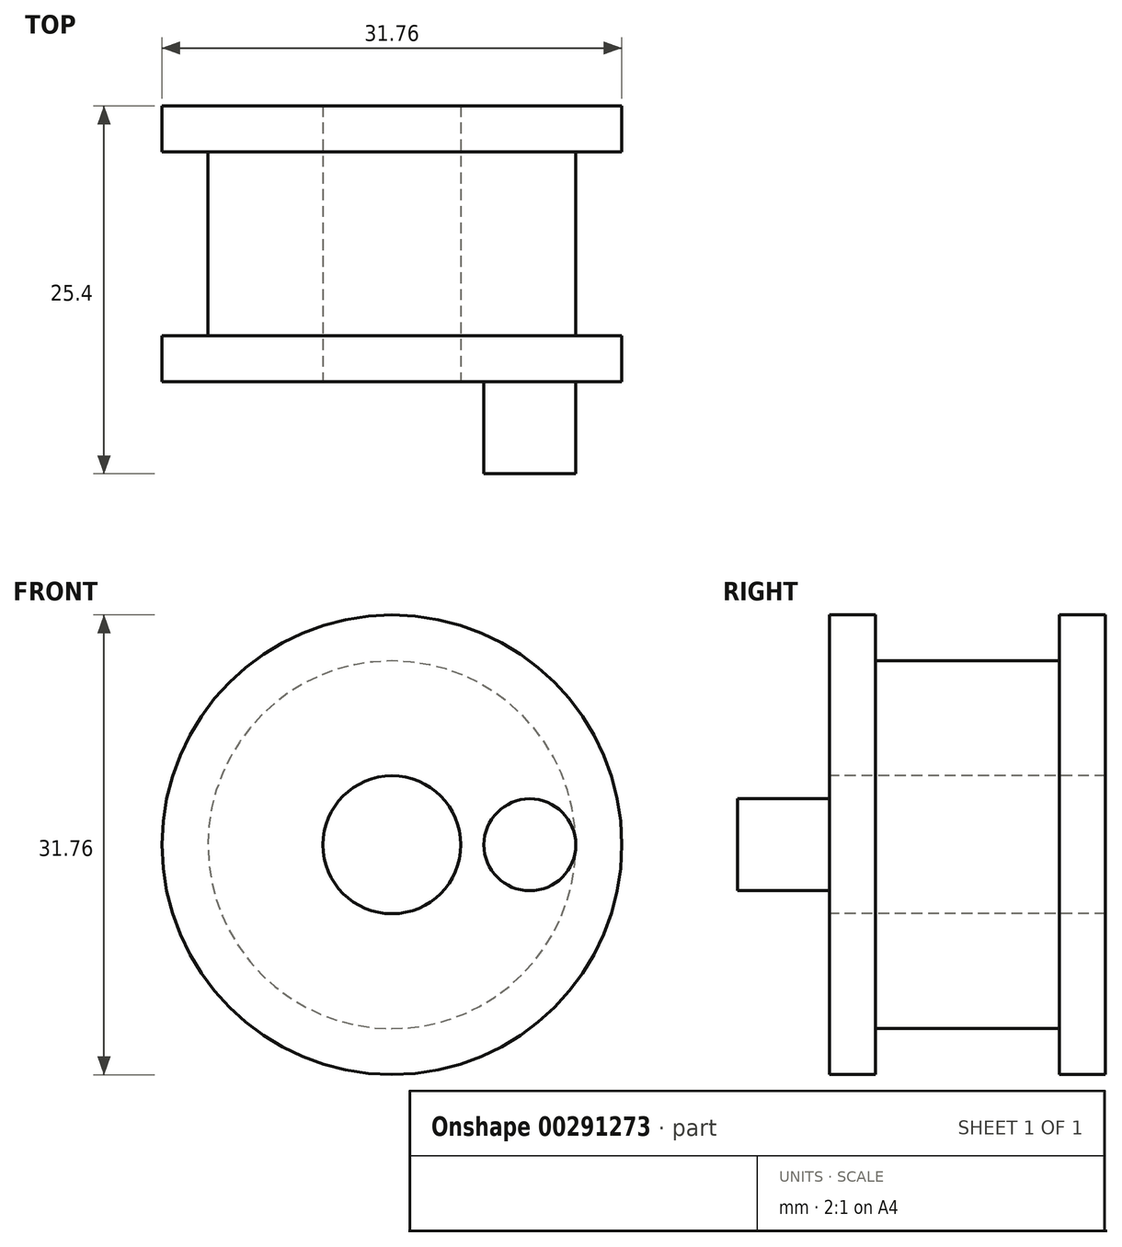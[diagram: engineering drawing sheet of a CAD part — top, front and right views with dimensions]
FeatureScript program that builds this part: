
annotation { "Feature Type Name" : "Feature", "Feature Type Description" : "" }
export const myFeature = defineFeature(function(context is Context, id is Id, definition is map)
    precondition{}
    {
        {
            var Q0;
            Q0=qCreatedBy(makeId("Right.planeOp"),FACE);
            var sketch = newSketch(context, id + "F0", { "sketchPlane" : qUnion([Q0])});
            skLineSegment(sketch, "E0", {"start": v(0, 0) * mm, "end": v(0, 4.76) * mm});
            skLineSegment(sketch, "E1", {"start": v(0, 4.76) * mm, "end": v(19.05, 4.76) * mm});
            skLineSegment(sketch, "E2", {"start": v(19.05, 4.76) * mm, "end": v(19.05, 15.88) * mm});
            skLineSegment(sketch, "E3", {"start": v(19.05, 15.88) * mm, "end": v(15.88, 15.88) * mm});
            skLineSegment(sketch, "E4", {"start": v(15.88, 15.88) * mm, "end": v(15.88, 12.7) * mm});
            skLineSegment(sketch, "E5", {"start": v(15.88, 12.7) * mm, "end": v(3.17, 12.7) * mm});
            skLineSegment(sketch, "E6", {"start": v(3.17, 12.7) * mm, "end": v(3.17, 15.88) * mm});
            skLineSegment(sketch, "E7", {"start": v(3.17, 15.88) * mm, "end": v(0, 15.88) * mm});
            skLineSegment(sketch, "E8", {"start": v(0, 15.88) * mm, "end": v(0, 4.76) * mm});
            skLineSegment(sketch, "E9", {"start": v(0, 0) * mm, "end": v(30.3, 0) * mm});
            skSolve(sketch);
        }
        {
            var Q0;
            Q0 = qSketchRegion(id + "F0", true);
            var Q1;
            Q1=sQuery(id+"F0.wireOp",EDGE,"E9");
            revolve(context, id + "F1", {"entities" : qUnion([Q0]), "axis" : qUnion([Q1]), "revolveType" : RevolveType.FULL});
        }
        {
            var Q0;
            Q0=qCreatedBy(makeId("Front.planeOp"),FACE);
            var sketch = newSketch(context, id + "F2", { "sketchPlane" : qUnion([Q0])});
            skCircle(sketch, "E10", {"center": v(9.53, 0) * mm, "radius": 3.18 * mm});
            skSolve(sketch);
        }
        {
            var Q0;
            Q0 = qSketchRegion(id + "F2", true);
            extrude(context, id + "F3", {"entities" : qUnion([Q0]), "operationType" : NewBodyOperationType.ADD, "depth" : 6.35 * mm});
        }
    });
